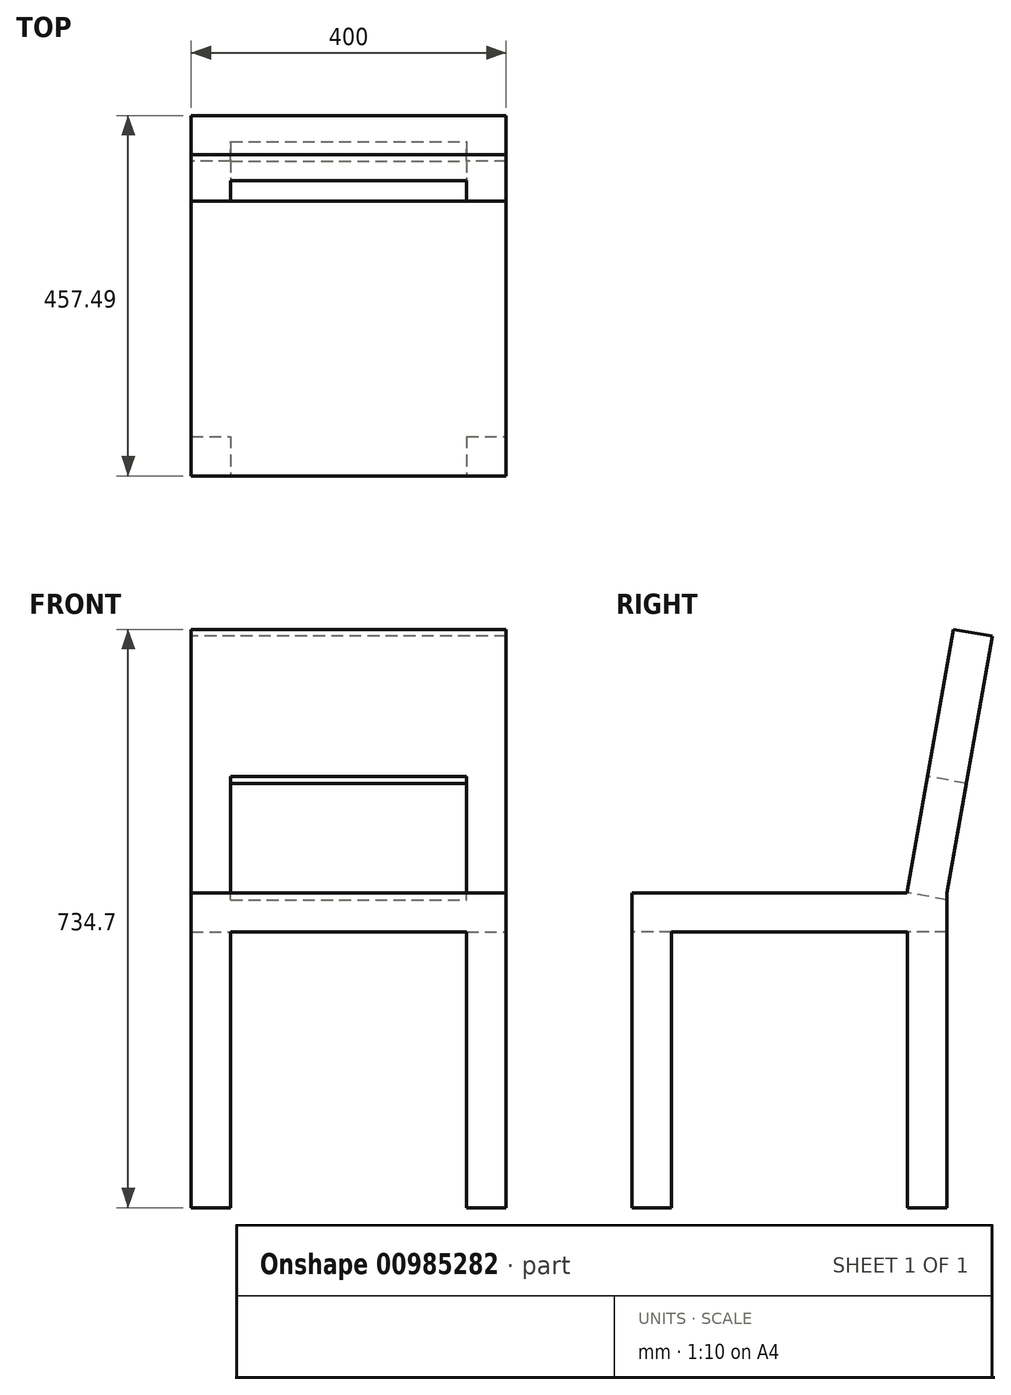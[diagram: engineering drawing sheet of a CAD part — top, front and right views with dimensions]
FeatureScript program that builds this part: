
annotation { "Feature Type Name" : "Feature", "Feature Type Description" : "" }
export const myFeature = defineFeature(function(context is Context, id is Id, definition is map)
    precondition{}
    {
        {
            var Q0;
            Q0=qCreatedBy(makeId("Top.planeOp"),FACE);
            var sketch = newSketch(context, id + "F0", { "sketchPlane" : qUnion([Q0])});
            skLineSegment(sketch, "E0.bottom", {"start": v(200, -200) * mm, "end": v(-200, -200) * mm});
            skLineSegment(sketch, "E0.top", {"start": v(200, 200) * mm, "end": v(-200, 200) * mm});
            skLineSegment(sketch, "E0.left", {"start": v(200, -200) * mm, "end": v(200, 200) * mm});
            skLineSegment(sketch, "E0.right", {"start": v(-200, -200) * mm, "end": v(-200, 200) * mm});
            skPoint(sketch, "E0.middle", {"position": v(0, 0) * mm});
            skSolve(sketch);
        }
        {
            var Q0;
            Q0 = qSketchRegion(id + "F0", true);
            extrude(context, id + "F1", {"entities" : qUnion([Q0]), "depth" : 400 * mm, "offsetDistance" : 25 * mm});
        }
        {
            var Q0;
            Q0=makeQuery(id+"F1.opExtrude","SWEPT_FACE",FACE,{"disambiguationData":[OSD([sQuery(id+"F0.wireOp",EDGE,"E0.bottom")])]});
            var sketch = newSketch(context, id + "F2", { "sketchPlane" : qUnion([Q0])});
            skLineSegment(sketch, "E1.bottom", {"start": v(-150, 0) * mm, "end": v(150, 0) * mm});
            skLineSegment(sketch, "E1.top", {"start": v(-150, 350) * mm, "end": v(150, 350) * mm});
            skLineSegment(sketch, "E1.left", {"start": v(-150, 0) * mm, "end": v(-150, 350) * mm});
            skLineSegment(sketch, "E1.right", {"start": v(150, 0) * mm, "end": v(150, 350) * mm});
            skSolve(sketch);
        }
        {
            var Q0;
            Q0=makeQuery(id+"F2.imprint","IMPRINT",FACE,{"disambiguationData":[TD([[makeQuery(id+"F2.imprint","IMPRINT",EDGE,{"derivedFrom":sQuery(id+"F2.wireOp",EDGE,"E1.bottom")}),-1.0]])]});
            extrude(context, id + "F3", {"entities" : qUnion([Q0]), "operationType" : NewBodyOperationType.REMOVE, "endBound" : BoundingType.THROUGH_ALL, "oppositeDirection" : true, "depth" : 25 * mm, "offsetDistance" : 25 * mm});
        }
        {
            var Q0;
            Q0=makeQuery(id+"F1.opExtrude","SWEPT_FACE",FACE,{"disambiguationData":[OSD([sQuery(id+"F0.wireOp",EDGE,"E0.left")])]});
            var sketch = newSketch(context, id + "F4", { "sketchPlane" : qUnion([Q0])});
            skLineSegment(sketch, "E2.bottom", {"start": v(-150, 0) * mm, "end": v(150, 0) * mm});
            skLineSegment(sketch, "E2.top", {"start": v(-150, 350) * mm, "end": v(150, 350) * mm});
            skLineSegment(sketch, "E2.left", {"start": v(-150, 0) * mm, "end": v(-150, 350) * mm});
            skLineSegment(sketch, "E2.right", {"start": v(150, 0) * mm, "end": v(150, 350) * mm});
            skSolve(sketch);
        }
        {
            var Q0;
            Q0=makeQuery(id+"F4.imprint","IMPRINT",FACE,{"disambiguationData":[TD([[makeQuery(id+"F4.imprint","IMPRINT",EDGE,{"derivedFrom":sQuery(id+"F4.wireOp",EDGE,"E2.bottom")}),1.0]])]});
            extrude(context, id + "F5", {"entities" : qUnion([Q0]), "operationType" : NewBodyOperationType.REMOVE, "endBound" : BoundingType.THROUGH_ALL, "oppositeDirection" : true, "depth" : 25 * mm, "offsetDistance" : 25 * mm});
        }
        {
            var Q0;
            Q0=makeQuery(id+"F1.opExtrude","CAP_FACE",FACE,{"disambiguationData":[OSD([sQuery(id+"F0.wireOp",EDGE,"E0.bottom"),sQuery(id+"F0.wireOp",EDGE,"E0.top"),sQuery(id+"F0.wireOp",EDGE,"E0.left"),sQuery(id+"F0.wireOp",EDGE,"E0.right")])],"isStart":false});
            var sketch = newSketch(context, id + "F6", { "sketchPlane" : qUnion([Q0])});
            skLineSegment(sketch, "E3", {"start": v(-252.73, 200) * mm, "end": v(340.36, 200) * mm});
            skSolve(sketch);
        }
        {
            var Q0;
            Q0=makeQuery(id+"F1.opExtrude","SWEPT_FACE",FACE,{"disambiguationData":[OSD([sQuery(id+"F0.wireOp",EDGE,"E0.top")])]});
            var Q1;
            Q1=sQuery(id+"F6.wireOp",EDGE,"E3");
            cPlane(context, id + "F7", {"entities" : qUnion([Q0, Q1]), "cplaneType" : CPlaneType.LINE_ANGLE, "offset" : 25 * mm, "angle" : 10 * degree, "oppositeDirection" : true, "width" : 150 * mm, "height" : 150 * mm});
        }
        {
            var Q0;
            Q0=qCreatedBy(id+"F7.planeOp",FACE);
            var sketch = newSketch(context, id + "F8", { "sketchPlane" : qUnion([Q0])});
            skLineSegment(sketch, "E4.bottom", {"start": v(200, 428.92) * mm, "end": v(-200, 428.92) * mm});
            skLineSegment(sketch, "E4.top", {"start": v(200, 759.7) * mm, "end": v(-200, 759.7) * mm});
            skLineSegment(sketch, "E4.left", {"start": v(200, 428.92) * mm, "end": v(200, 759.7) * mm});
            skLineSegment(sketch, "E4.right", {"start": v(-200, 428.92) * mm, "end": v(-200, 759.7) * mm});
            skSolve(sketch);
        }
        {
            var Q0;
            Q0 = qSketchRegion(id + "F8", true);
            extrude(context, id + "F9", {"entities" : qUnion([Q0]), "depth" : 50 * mm, "offsetDistance" : 25 * mm});
        }
        {
            var Q0;
            Q0=makeQuery(id+"F9.opExtrude","SWEPT_FACE",FACE,{"disambiguationData":[OSD([sQuery(id+"F8.wireOp",EDGE,"E4.bottom")])]});
            extrude(context, id + "F10", {"entities" : qUnion([Q0]), "operationType" : NewBodyOperationType.ADD, "endBound" : BoundingType.UP_TO_NEXT, "depth" : 25 * mm, "offsetDistance" : 25 * mm});
        }
        {
            var Q0;
            {var subQ0=sQuery(id+"F8.wireOp",EDGE,"E4.bottom");Q0=makeQuery(id+"F10.boolean.opBoolean","MERGE",FACE,{"derivedFrom":[makeQuery(id+"F9.opExtrude","CAP_FACE",FACE,{"disambiguationData":[OSD([subQ0,sQuery(id+"F8.wireOp",EDGE,"E4.top"),sQuery(id+"F8.wireOp",EDGE,"E4.left"),sQuery(id+"F8.wireOp",EDGE,"E4.right")])],"isStart":false}),makeQuery(id+"F10.opExtrude","SWEPT_FACE",FACE,{"disambiguationData":[OSD([subQ0]),TDD([makeQuery(id+"F9.opExtrude","CAP_EDGE",EDGE,{"disambiguationData":[OSD([subQ0])],"isStart":false})])]})]});}
            var sketch = newSketch(context, id + "F11", { "sketchPlane" : qUnion([Q0])});
            skLineSegment(sketch, "E5.bottom", {"start": v(-150, 419.84) * mm, "end": v(150, 419.84) * mm});
            skLineSegment(sketch, "E5.top", {"start": v(-150, 569.84) * mm, "end": v(150, 569.84) * mm});
            skLineSegment(sketch, "E5.left", {"start": v(-150, 419.84) * mm, "end": v(-150, 569.84) * mm});
            skLineSegment(sketch, "E5.right", {"start": v(150, 419.84) * mm, "end": v(150, 569.84) * mm});
            skSolve(sketch);
        }
        {
            var Q0;
            Q0=makeQuery(id+"F11.imprint","IMPRINT",FACE,{"disambiguationData":[TD([[makeQuery(id+"F11.imprint","IMPRINT",EDGE,{"derivedFrom":sQuery(id+"F11.wireOp",EDGE,"E5.bottom")}),1.0]])]});
            extrude(context, id + "F12", {"entities" : qUnion([Q0]), "operationType" : NewBodyOperationType.REMOVE, "endBound" : BoundingType.THROUGH_ALL, "oppositeDirection" : true, "depth" : 245 * mm, "offsetDistance" : 25 * mm});
        }
    });
